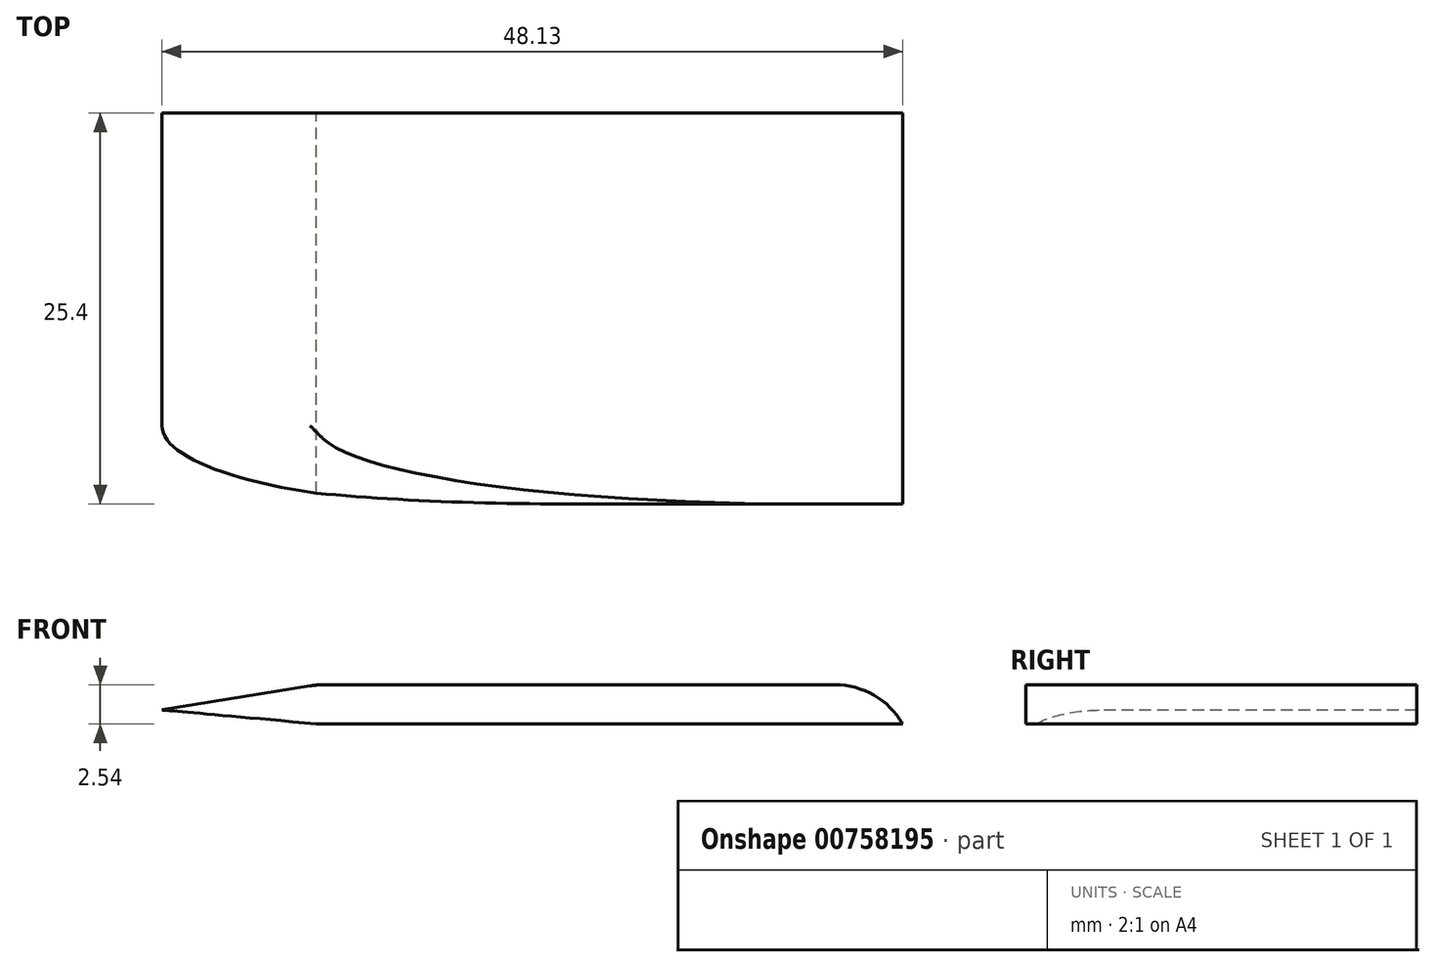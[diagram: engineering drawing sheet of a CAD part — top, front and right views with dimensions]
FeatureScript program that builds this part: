
annotation { "Feature Type Name" : "Feature", "Feature Type Description" : "" }
export const myFeature = defineFeature(function(context is Context, id is Id, definition is map)
    precondition{}
    {
        {
            var Q0;
            Q0=qCreatedBy(makeId("Front.planeOp"),FACE);
            var sketch = newSketch(context, id + "F0", { "sketchPlane" : qUnion([Q0])});
            skLineSegment(sketch, "E0", {"start": v(-17.73, 0) * mm, "end": v(-7.7, 1.63) * mm});
            skLineSegment(sketch, "E1", {"start": v(-7.7, 1.63) * mm, "end": v(30.4, 1.63) * mm});
            skLineSegment(sketch, "E2", {"start": v(30.4, 1.63) * mm, "end": v(30.4, -0.91) * mm});
            skLineSegment(sketch, "E3", {"start": v(30.4, -0.91) * mm, "end": v(-7.7, -0.91) * mm});
            skLineSegment(sketch, "E4", {"start": v(-7.7, -0.91) * mm, "end": v(-17.73, 0) * mm});
            skSolve(sketch);
        }
        {
            var Q0;
            Q0=makeQuery(id+"F0.imprint","IMPRINT",FACE,{"disambiguationData":[TD([[makeQuery(id+"F0.imprint","IMPRINT",EDGE,{"derivedFrom":sQuery(id+"F0.wireOp",EDGE,"E0")}),-1.0]])]});
            extrude(context, id + "F1", {"entities" : qUnion([Q0]), "depth" : 25.4 * mm, "offsetDistance" : 25.4 * mm});
        }
        {
            var Q0;
            Q0=makeQuery(id+"F1.opExtrude","CAP_EDGE",EDGE,{"disambiguationData":[OSD([sQuery(id+"F0.wireOp",EDGE,"E0")])],"isStart":false});
            var Q1;
            Q1=makeQuery(id+"F1.opExtrude","SWEPT_EDGE",EDGE,{"disambiguationData":[OSD([sQuery(id+"F0.wireOp",EDGE,"E0"),sQuery(id+"F0.wireOp",EDGE,"E1")])]});
            var Q2;
            Q2=makeQuery(id+"F1.opExtrude","SWEPT_EDGE",EDGE,{"disambiguationData":[OSD([sQuery(id+"F0.wireOp",EDGE,"E1"),sQuery(id+"F0.wireOp",EDGE,"E2")])]});
            fillet(context, id + "F2", {"entities" : qUnion([Q0, Q1, Q2]), "radius" : 5.08 * mm, "tangentPropagation" : true, "allowEdgeOverflow" : false});
        }
    });
